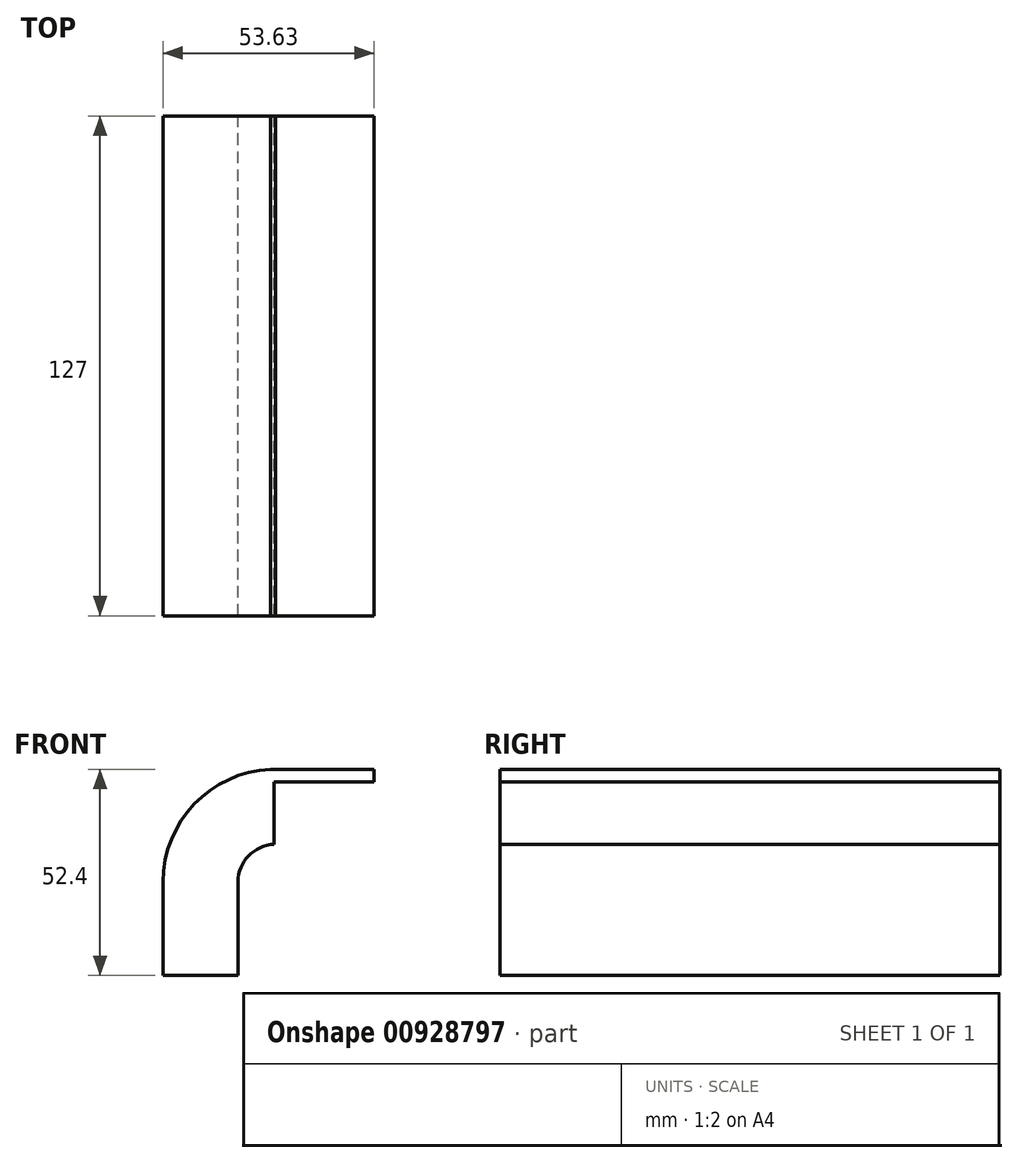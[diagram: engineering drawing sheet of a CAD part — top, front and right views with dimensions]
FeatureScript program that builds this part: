
annotation { "Feature Type Name" : "Feature", "Feature Type Description" : "" }
export const myFeature = defineFeature(function(context is Context, id is Id, definition is map)
    precondition{}
    {
        {
            var Q0;
            Q0=qCreatedBy(makeId("Front.planeOp"),FACE);
            var sketch = newSketch(context, id + "F0", { "sketchPlane" : qUnion([Q0])});
            skLineSegment(sketch, "E0.bottom", {"start": v(-41.28, 9.52) * mm, "end": v(41.27, 9.53) * mm});
            skLineSegment(sketch, "E0.top", {"start": v(-41.28, -9.53) * mm, "end": v(41.28, -9.53) * mm});
            skLineSegment(sketch, "E0.left", {"start": v(-41.28, 9.52) * mm, "end": v(-41.27, -9.53) * mm});
            skLineSegment(sketch, "E0.right", {"start": v(41.28, 9.53) * mm, "end": v(41.28, -9.52) * mm});
            skPoint(sketch, "E0.middle", {"position": v(0, 0) * mm});
            skLineSegment(sketch, "E1.bottom", {"start": v(101.25, 27) * mm, "end": v(50.45, 27) * mm});
            skLineSegment(sketch, "E1.top", {"start": v(101.25, 58.75) * mm, "end": v(50.45, 58.75) * mm});
            skLineSegment(sketch, "E1.left", {"start": v(101.25, 27) * mm, "end": v(101.25, 58.75) * mm});
            skLineSegment(sketch, "E1.right", {"start": v(50.45, 27) * mm, "end": v(50.45, 58.75) * mm});
            skPoint(sketch, "E1.middle", {"position": v(75.85, 42.88) * mm});
            skLineSegment(sketch, "E2", {"start": v(41.27, 9.53) * mm, "end": v(41.27, 33.33) * mm});
            skArc(sketch, "E3", {"start": v(41.27, 33.33) * mm, "mid": v(44.07, 40.08) * mm, "end": v(50.82, 42.88) * mm});
            skLineSegment(sketch, "E4", {"start": v(50.82, 42.88) * mm, "end": v(75.85, 42.88) * mm});
            skLineSegment(sketch, "E5.0", {"start": v(50.82, 61.93) * mm, "end": v(75.85, 61.93) * mm});
            skArc(sketch, "E5.1", {"start": v(22.22, 33.33) * mm, "mid": v(30.6, 53.55) * mm, "end": v(50.82, 61.93) * mm});
            skLineSegment(sketch, "E5.2", {"start": v(22.22, 9.53) * mm, "end": v(22.22, 33.33) * mm});
            skFitSpline(sketch, "E6", {"points": [v(-41.28, 9.52) * mm, v(50.82, 61.93) * mm], "startDerivative": vector(1.21, 63.85) * mm, "endDerivative": vector(124.32, 1.89) * mm});
            skLineSegment(sketch, "E7", {"start": v(75.85, 61.93) * mm, "end": v(75.85, 27) * mm});
            skSolve(sketch);
        }
        {
            var Q0;
            {var subQ0=sQuery(id+"F0.wireOp",EDGE,"E2");Q0=makeQuery(id+"F0.imprint","IMPRINT",FACE,{"disambiguationData":[TD([[makeQuery(id+"F0.imprint","IMPRINT",EDGE,{"derivedFrom":subQ0}),1.0]])]});}
            extrude(context, id + "F1", {"entities" : qUnion([Q0]), "endBound" : BoundingType.SYMMETRIC, "depth" : 127 * mm, "offsetDistance" : 25.4 * mm});
        }
    });
